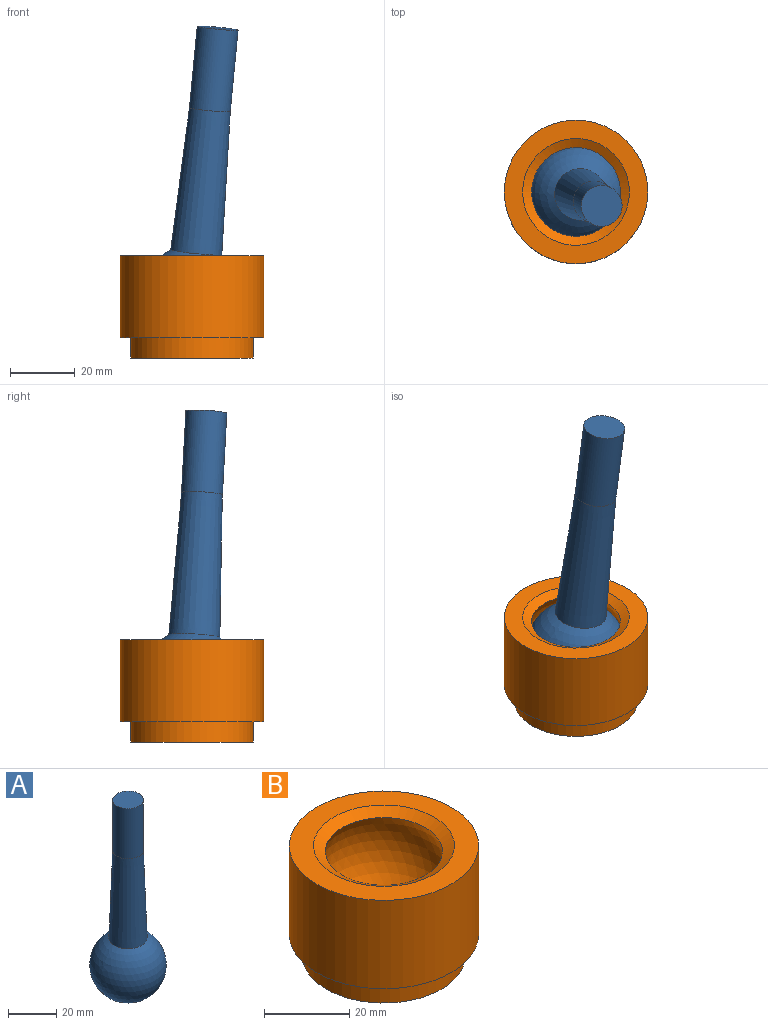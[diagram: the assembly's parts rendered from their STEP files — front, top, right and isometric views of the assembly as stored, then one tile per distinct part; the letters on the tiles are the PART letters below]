
ASSEMBLY  parts=2 mates=1
PART A: 4 faces, bbox 31.8x31.8x99.5 mm
  f0: plane 12.7x12.7mm, normal (0,0,1), area 126.7mm2, adj f3
  f1: sphere r=15.88mm, area 2954.8mm2, adj f2
  f2: cone r=7.94mm half-angle=2deg, axis (0,0,-1), area 1996.4mm2, adj f1,f3
  f3: cylinder r=6.35mm len=25.4mm, axis (0,0,-1), area 1013.4mm2, adj f0,f2
PART B: 7 faces, bbox 44.5x44.5x31.8 mm
  f0: cylinder r=22.23mm len=44.45mm, axis (0,0,-1), area 3547mm2, adj f2,f5
  f1: sphere r=15.88mm, area 2375.2mm2, adj f3
  f2: plane 44.45x44.45mm, normal (0,0,1), area 693.1mm2, adj f0,f3
  f3: cone r=13.75mm half-angle=59.2deg, axis (0,0,1), area 308.5mm2, adj f1,f2
  f4: cylinder r=19.05mm len=38.1mm, axis (0,0,-1), area 760.1mm2, adj f5,f6
  f5: plane 44.45x44.45mm, normal (0,0,-1), area 411.7mm2, adj f0,f4
  f6: plane 38.1x38.1mm, normal (0,0,-1), area 1140.1mm2, adj f4
PLACE A rot(axis=(0.49,0.87,-0.05),6.2deg) t=(-25.02,24.37,-40.29)mm
PLACE B t=(-25.02,24.37,-37.19)mm fixed
MATE ball A.f2 <-> B.f3  axis (0.09,-0.05,0.99) through (-25.02,24.37,-40.29)mm
